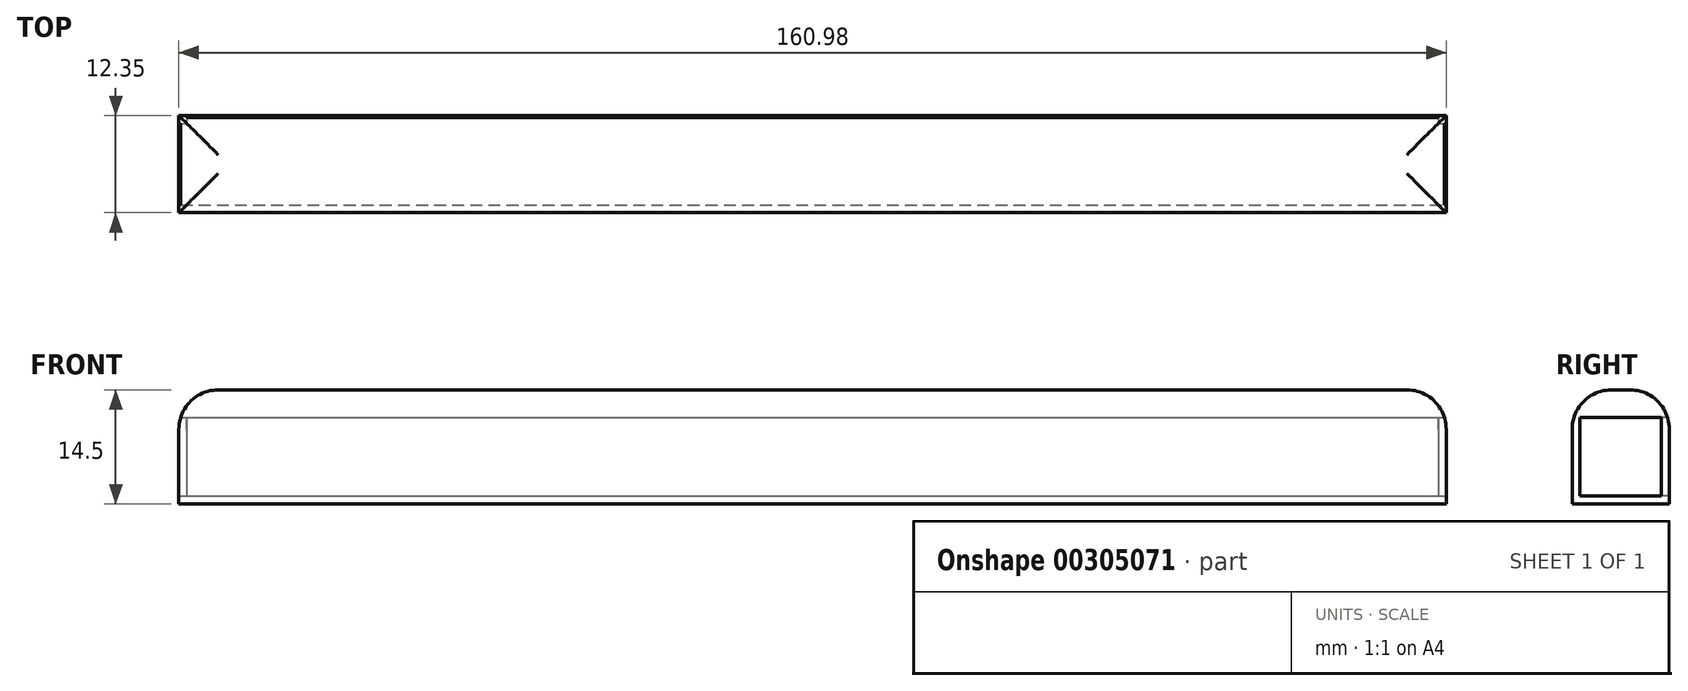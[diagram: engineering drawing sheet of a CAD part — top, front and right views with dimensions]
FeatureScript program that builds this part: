
annotation { "Feature Type Name" : "Feature", "Feature Type Description" : "" }
export const myFeature = defineFeature(function(context is Context, id is Id, definition is map)
    precondition{}
    {
        {
            var Q0;
            Q0=qCreatedBy(makeId("Top.planeOp"),FACE);
            var sketch = newSketch(context, id + "F0", { "sketchPlane" : qUnion([Q0])});
            skLineSegment(sketch, "E0.bottom", {"start": v(-72.66, 5.13) * mm, "end": v(88.32, 5.13) * mm});
            skLineSegment(sketch, "E0.top", {"start": v(-72.66, -7.22) * mm, "end": v(88.32, -7.22) * mm});
            skLineSegment(sketch, "E0.left", {"start": v(-72.66, 5.13) * mm, "end": v(-72.66, -7.22) * mm});
            skLineSegment(sketch, "E0.right", {"start": v(88.32, 5.13) * mm, "end": v(88.32, -7.22) * mm});
            skSolve(sketch);
        }
        {
            var Q0;
            Q0=makeQuery(id+"F0.imprint","IMPRINT",FACE,{"disambiguationData":[TD([[makeQuery(id+"F0.imprint","IMPRINT",EDGE,{"derivedFrom":sQuery(id+"F0.wireOp",EDGE,"E0.bottom")}),-1.0]])]});
            extrude(context, id + "F1", {"entities" : qUnion([Q0]), "depth" : 12 * mm});
        }
        {
            var Q0;
            Q0=makeQuery(id+"F1.opExtrude","SWEPT_FACE",FACE,{"disambiguationData":[OSD([sQuery(id+"F0.wireOp",EDGE,"E0.bottom")])]});
            shell(context, id + "F2", {"entities" : qUnion([Q0]), "thickness" : 1 * mm});
        }
        {
            var Q0;
            Q0=makeQuery(id+"F2.opShell","OFFSET_FACE",FACE,{"disambiguationData":[OSD([sQuery(id+"F0.wireOp",EDGE,"E0.right")])]});
            var Q1;
            Q1=makeQuery(id+"F1.opExtrude","SWEPT_FACE",FACE,{"disambiguationData":[OSD([sQuery(id+"F0.wireOp",EDGE,"E0.right")])]});
            shell(context, id + "F3", {"entities" : qUnion([Q0, Q1]), "thickness" : 1 * mm});
        }
        {
            var Q0;
            Q0=makeQuery(id+"F1.opExtrude","SWEPT_FACE",FACE,{"disambiguationData":[OSD([sQuery(id+"F0.wireOp",EDGE,"E0.left")])]});
            var Q1;
            Q1=makeQuery(id+"F2.opShell","OFFSET_FACE",FACE,{"disambiguationData":[OSD([sQuery(id+"F0.wireOp",EDGE,"E0.left")])]});
            shell(context, id + "F4", {"entities" : qUnion([Q0, Q1]), "thickness" : 1 * mm});
        }
        {
            var Q0;
            Q0=makeQuery(id+"F1.opExtrude","CAP_FACE",FACE,{"disambiguationData":[OSD([sQuery(id+"F0.wireOp",EDGE,"E0.bottom"),sQuery(id+"F0.wireOp",EDGE,"E0.top"),sQuery(id+"F0.wireOp",EDGE,"E0.left"),sQuery(id+"F0.wireOp",EDGE,"E0.right")])],"isStart":false});
            extrude(context, id + "F5", {"entities" : qUnion([Q0]), "operationType" : NewBodyOperationType.ADD, "depth" : 2.5 * mm});
        }
        {
            var Q0;
            {var subQ0=sQuery(id+"F0.wireOp",EDGE,"E0.right");var subQ1=sQuery(id+"F0.wireOp",EDGE,"E0.left");var subQ2=sQuery(id+"F0.wireOp",EDGE,"E0.top");var subQ3=sQuery(id+"F0.wireOp",EDGE,"E0.bottom");Q0=makeQuery(id+"F5.opExtrude","CAP_FACE",FACE,{"disambiguationData":[OSD([subQ3,subQ2,subQ1,subQ0]),TDD([makeQuery(id+"F1.opExtrude","CAP_FACE",FACE,{"disambiguationData":[OSD([subQ3,subQ2,subQ1,subQ0])],"isStart":false})])],"isStart":false});}
            fillet(context, id + "F6", {"entities" : qUnion([Q0]), "radius" : 5 * mm, "tangentPropagation" : true, "allowEdgeOverflow" : false});
        }
    });
